# Revit family: AD-C42T
name_source: partatom
category: Communication Devices
revit_build: Autodesk Revit 2014 (Build: 20130308_1515(x64)
units: mm (PartAtom-declared; Revit-internal decimal feet)

## types (1)
- AD-C42T
    100V Taps = 16, 8, 4, 2
    70V Taps = 16, 8, 4, 2, 1
    Coverage Horizontal = 140.00°
    Coverage Vertical = 140.00°
    Default Elevation = 0"
    Depth = 7.91"
    Description = 4" Full-Range Wide Coverage Loudspeaker
    Enclosure Depth = 6.52"
    Enclosure Radius = 3.575"
    Grille Depth = 0.39"
    Grille Radius Base = 4.215"
    Grille Radius Extent = 4"
    Impedance = 8
    Manufacturer = QSC Audio Products, LLC
    Manufacturer URL = www.qscaudio.com
    Middle Depth = 1"
    Middle Radius = 4.09"
    Model = AC-C4T
    Power Handling = 16
    Product Documentation Link = http://www.qsc.com
    Product Page URL = http://www.qsc.com
    Regulatory Compliance = UL1480, UL2043
    SPL Max = 107
    Sensitivity = 89
    URL = http://www.qscaudio.com
    Weight Dimensional (kg) = 6.86
    Weight Dimensional (lb) = 15.1
    Weight Product (kg) = 2.22
    Weight Product (lb) = 4.9
    Width = 8.43"

## geometry (parser evidence)
native form markers: Blend x7, Sweep x1
no freeform markers — native parametric forms only
